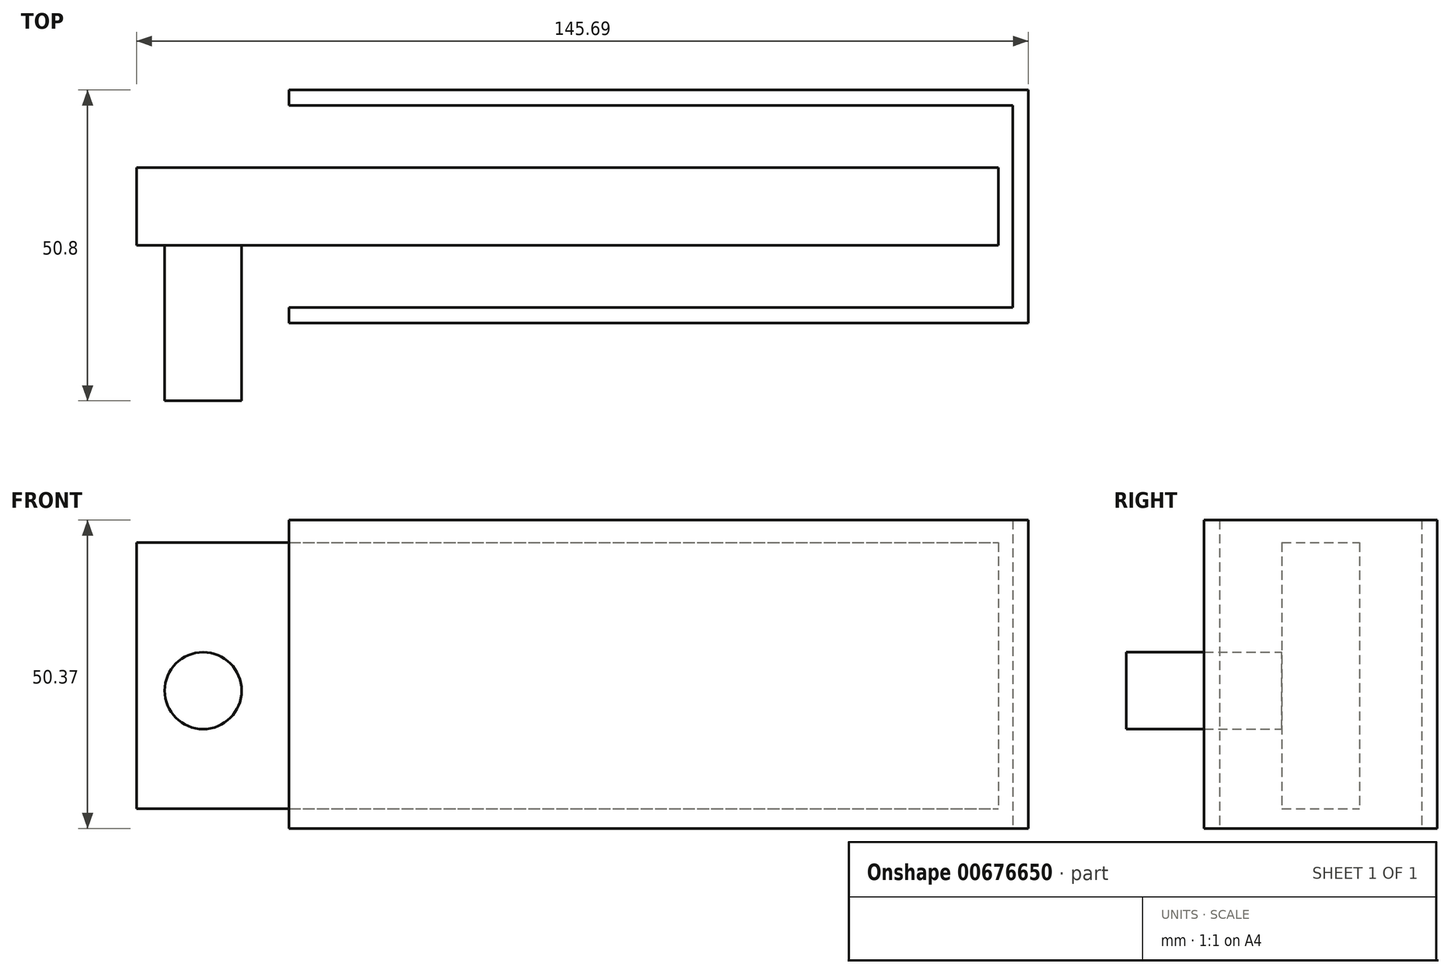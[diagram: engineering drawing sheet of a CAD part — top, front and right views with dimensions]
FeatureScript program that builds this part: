
annotation { "Feature Type Name" : "Feature", "Feature Type Description" : "" }
export const myFeature = defineFeature(function(context is Context, id is Id, definition is map)
    precondition{}
    {
        {
            var Q0;
            Q0=qCreatedBy(makeId("Front.planeOp"),FACE);
            var sketch = newSketch(context, id + "F0", { "sketchPlane" : qUnion([Q0])});
            skLineSegment(sketch, "E0.bottom", {"start": v(-73.78, 27.86) * mm, "end": v(47.03, 27.86) * mm});
            skLineSegment(sketch, "E0.top", {"start": v(-73.78, -22.51) * mm, "end": v(47.03, -22.51) * mm});
            skLineSegment(sketch, "E0.left", {"start": v(-73.78, 27.86) * mm, "end": v(-73.78, -22.51) * mm});
            skLineSegment(sketch, "E0.right", {"start": v(47.03, 27.86) * mm, "end": v(47.03, -22.51) * mm});
            skSolve(sketch);
        }
        {
            var Q0;
            Q0 = qSketchRegion(id + "F0", true);
            extrude(context, id + "F1", {"entities" : qUnion([Q0]), "depth" : 25.4 * mm, "offsetDistance" : 25.4 * mm});
        }
        {
            var Q0;
            Q0=makeQuery(id+"F1.opExtrude","CAP_FACE",FACE,{"disambiguationData":[OSD([sQuery(id+"F0.wireOp",EDGE,"E0.bottom"),sQuery(id+"F0.wireOp",EDGE,"E0.top"),sQuery(id+"F0.wireOp",EDGE,"E0.left"),sQuery(id+"F0.wireOp",EDGE,"E0.right")])],"isStart":true});
            extrude(context, id + "F2", {"entities" : qUnion([Q0]), "operationType" : NewBodyOperationType.ADD, "endBound" : BoundingType.SYMMETRIC, "depth" : 25.4 * mm, "offsetDistance" : 25.4 * mm});
        }
        {
            var Q0;
            {var subQ0=sQuery(id+"F0.wireOp",EDGE,"E0.bottom");Q0=makeQuery(id+"F2.boolean.opBoolean","MERGE",FACE,{"derivedFrom":[makeQuery(id+"F1.opExtrude","SWEPT_FACE",FACE,{"disambiguationData":[OSD([subQ0])]}),makeQuery(id+"F2.opExtrude","SWEPT_FACE",FACE,{"disambiguationData":[OSD([subQ0])]})]});}
            var Q1;
            {var subQ0=sQuery(id+"F0.wireOp",EDGE,"E0.left");Q1=makeQuery(id+"F2.boolean.opBoolean","MERGE",FACE,{"derivedFrom":[makeQuery(id+"F1.opExtrude","SWEPT_FACE",FACE,{"disambiguationData":[OSD([subQ0])]}),makeQuery(id+"F2.opExtrude","SWEPT_FACE",FACE,{"disambiguationData":[OSD([subQ0])]})]});}
            var Q2;
            {var subQ0=sQuery(id+"F0.wireOp",EDGE,"E0.top");Q2=makeQuery(id+"F2.boolean.opBoolean","MERGE",FACE,{"derivedFrom":[makeQuery(id+"F1.opExtrude","SWEPT_FACE",FACE,{"disambiguationData":[OSD([subQ0])]}),makeQuery(id+"F2.opExtrude","SWEPT_FACE",FACE,{"disambiguationData":[OSD([subQ0])]})]});}
            shell(context, id + "F3", {"entities" : qUnion([Q0, Q1, Q2]), "thickness" : 2.54 * mm});
        }
        {
            var Q0;
            Q0=qCreatedBy(makeId("Front.planeOp"),FACE);
            var sketch = newSketch(context, id + "F4", { "sketchPlane" : qUnion([Q0])});
            skLineSegment(sketch, "E1.bottom", {"start": v(-98.66, 24.2) * mm, "end": v(42.1, 24.2) * mm});
            skLineSegment(sketch, "E1.top", {"start": v(-98.66, -19.33) * mm, "end": v(42.1, -19.33) * mm});
            skLineSegment(sketch, "E1.left", {"start": v(-98.66, 24.2) * mm, "end": v(-98.66, -19.33) * mm});
            skLineSegment(sketch, "E1.right", {"start": v(42.1, 24.2) * mm, "end": v(42.1, -19.33) * mm});
            skSolve(sketch);
        }
        {
            var Q0;
            Q0 = qSketchRegion(id + "F4", true);
            extrude(context, id + "F5", {"entities" : qUnion([Q0]), "depth" : 12.7 * mm, "offsetDistance" : 25.4 * mm});
        }
        {
            var Q0;
            Q0=makeQuery(id+"F5.opExtrude","CAP_FACE",FACE,{"disambiguationData":[OSD([sQuery(id+"F4.wireOp",EDGE,"E1.bottom"),sQuery(id+"F4.wireOp",EDGE,"E1.top"),sQuery(id+"F4.wireOp",EDGE,"E1.left"),sQuery(id+"F4.wireOp",EDGE,"E1.right")])],"isStart":false});
            var sketch = newSketch(context, id + "F6", { "sketchPlane" : qUnion([Q0])});
            skCircle(sketch, "E2", {"center": v(-87.8, 0) * mm, "radius": 6.28 * mm});
            skSolve(sketch);
        }
        {
            var Q0;
            Q0=makeQuery(id+"F6.imprint","IMPRINT",FACE,{"disambiguationData":[TD([[makeQuery(id+"F6.imprint","IMPRINT",EDGE,{"derivedFrom":sQuery(id+"F6.wireOp",EDGE,"E2")}),1.0]])]});
            extrude(context, id + "F7", {"entities" : qUnion([Q0]), "operationType" : NewBodyOperationType.ADD, "depth" : 25.4 * mm, "offsetDistance" : 25.4 * mm});
        }
    });
